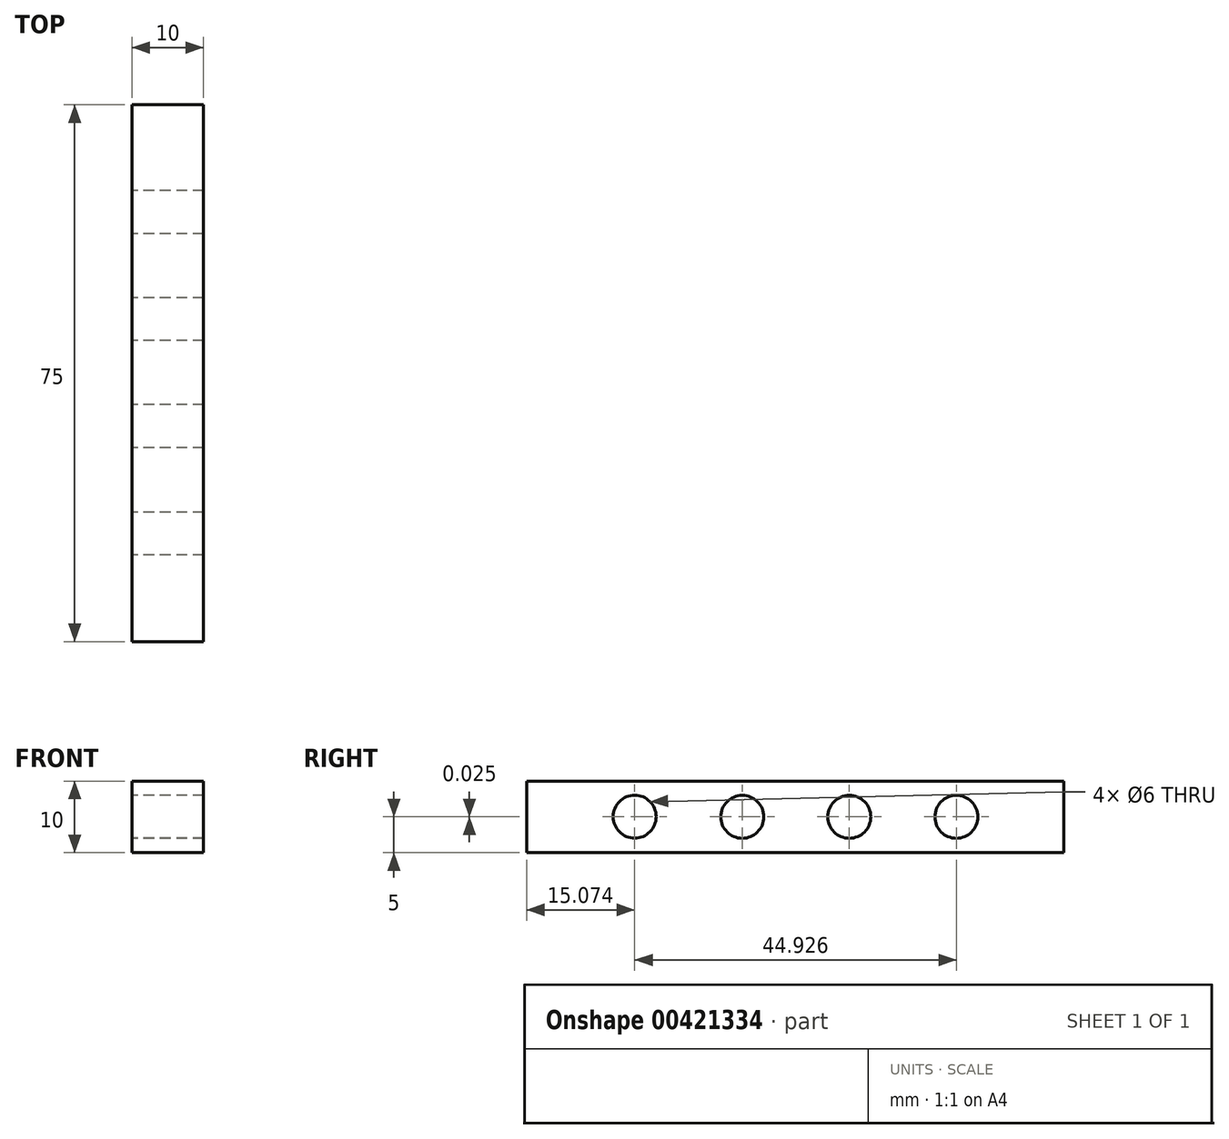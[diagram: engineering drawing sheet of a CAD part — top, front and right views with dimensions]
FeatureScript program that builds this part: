
annotation { "Feature Type Name" : "Feature", "Feature Type Description" : "" }
export const myFeature = defineFeature(function(context is Context, id is Id, definition is map)
    precondition{}
    {
        {
            var Q0;
            Q0=qCreatedBy(makeId("Front.planeOp"),FACE);
            var sketch = newSketch(context, id + "F0", { "sketchPlane" : qUnion([Q0])});
            skLineSegment(sketch, "E0.bottom", {"start": v(5, 5) * mm, "end": v(-5, 5) * mm});
            skLineSegment(sketch, "E0.top", {"start": v(5, -5) * mm, "end": v(-5, -5) * mm});
            skLineSegment(sketch, "E0.left", {"start": v(5, 5) * mm, "end": v(5, -5) * mm});
            skLineSegment(sketch, "E0.right", {"start": v(-5, 5) * mm, "end": v(-5, -5) * mm});
            skPoint(sketch, "E0.middle", {"position": v(0, 0) * mm});
            skSolve(sketch);
        }
        {
            var Q0;
            Q0=makeQuery(id+"F0.imprint","IMPRINT",FACE,{"disambiguationData":[TD([[makeQuery(id+"F0.imprint","IMPRINT",EDGE,{"derivedFrom":sQuery(id+"F0.wireOp",EDGE,"E0.bottom")}),1.0]])]});
            extrude(context, id + "F1", {"entities" : qUnion([Q0]), "depth" : 75 * mm});
        }
        {
            var Q0;
            Q0=makeQuery(id+"F1.opExtrude","SWEPT_FACE",FACE,{"disambiguationData":[OSD([sQuery(id+"F0.wireOp",EDGE,"E0.right")])]});
            var sketch = newSketch(context, id + "F2", { "sketchPlane" : qUnion([Q0])});
            skCircle(sketch, "E1", {"center": v(15, 0) * mm, "radius": 3 * mm});
            skCircle(sketch, "E2", {"center": v(29.96, 0) * mm, "radius": 3 * mm});
            skCircle(sketch, "E3", {"center": v(44.9, 0) * mm, "radius": 3 * mm});
            skCircle(sketch, "E4", {"center": v(59.93, 0.03) * mm, "radius": 3 * mm});
            skSolve(sketch);
        }
        {
            var Q0;
            Q0=makeQuery(id+"F2.imprint","IMPRINT",FACE,{"disambiguationData":[TD([[makeQuery(id+"F2.imprint","IMPRINT",EDGE,{"derivedFrom":sQuery(id+"F2.wireOp",EDGE,"E1")}),1.0]])]});
            var Q1;
            Q1=makeQuery(id+"F2.imprint","IMPRINT",FACE,{"disambiguationData":[TD([[makeQuery(id+"F2.imprint","IMPRINT",EDGE,{"derivedFrom":sQuery(id+"F2.wireOp",EDGE,"E2")}),1.0]])]});
            var Q2;
            Q2=makeQuery(id+"F2.imprint","IMPRINT",FACE,{"disambiguationData":[TD([[makeQuery(id+"F2.imprint","IMPRINT",EDGE,{"derivedFrom":sQuery(id+"F2.wireOp",EDGE,"E3")}),1.0]])]});
            var Q3;
            Q3=makeQuery(id+"F2.imprint","IMPRINT",FACE,{"disambiguationData":[TD([[makeQuery(id+"F2.imprint","IMPRINT",EDGE,{"derivedFrom":sQuery(id+"F2.wireOp",EDGE,"E4")}),1.0]])]});
            extrude(context, id + "F3", {"entities" : qUnion([Q0, Q1, Q2, Q3]), "operationType" : NewBodyOperationType.REMOVE, "oppositeDirection" : true, "depth" : 25 * mm});
        }
    });
